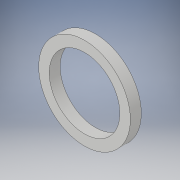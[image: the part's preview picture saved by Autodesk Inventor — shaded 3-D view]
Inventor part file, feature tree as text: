
AUTODESK INVENTOR PART (.ipt)
format: ipt  version: 2019 (Build 230136000, 136)  size: 103,424 bytes
history: native  units: mm
features: extrude x2, sketch x2
ambient origin geometry x8: Origin, YZ Plane, XZ Plane, XY Plane, X Axis, Y Axis, Z Axis, Center Point
bodies: Solid1 (feature_tree)
feature tree (4):
  extrude  "Extrusion1"  Depth=41.1mm TaperAngle=0.0deg
  extrude  "Extrusion2"  Depth=4.11mm TaperAngle=0.0deg
  sketch  "Sketch1"  dims[d0=344.0mm d1=41.1mm d2=0.0mm]
  sketch  "Sketch2"  dims[d3=265.0mm d4=4.11mm d5=0.0mm]
